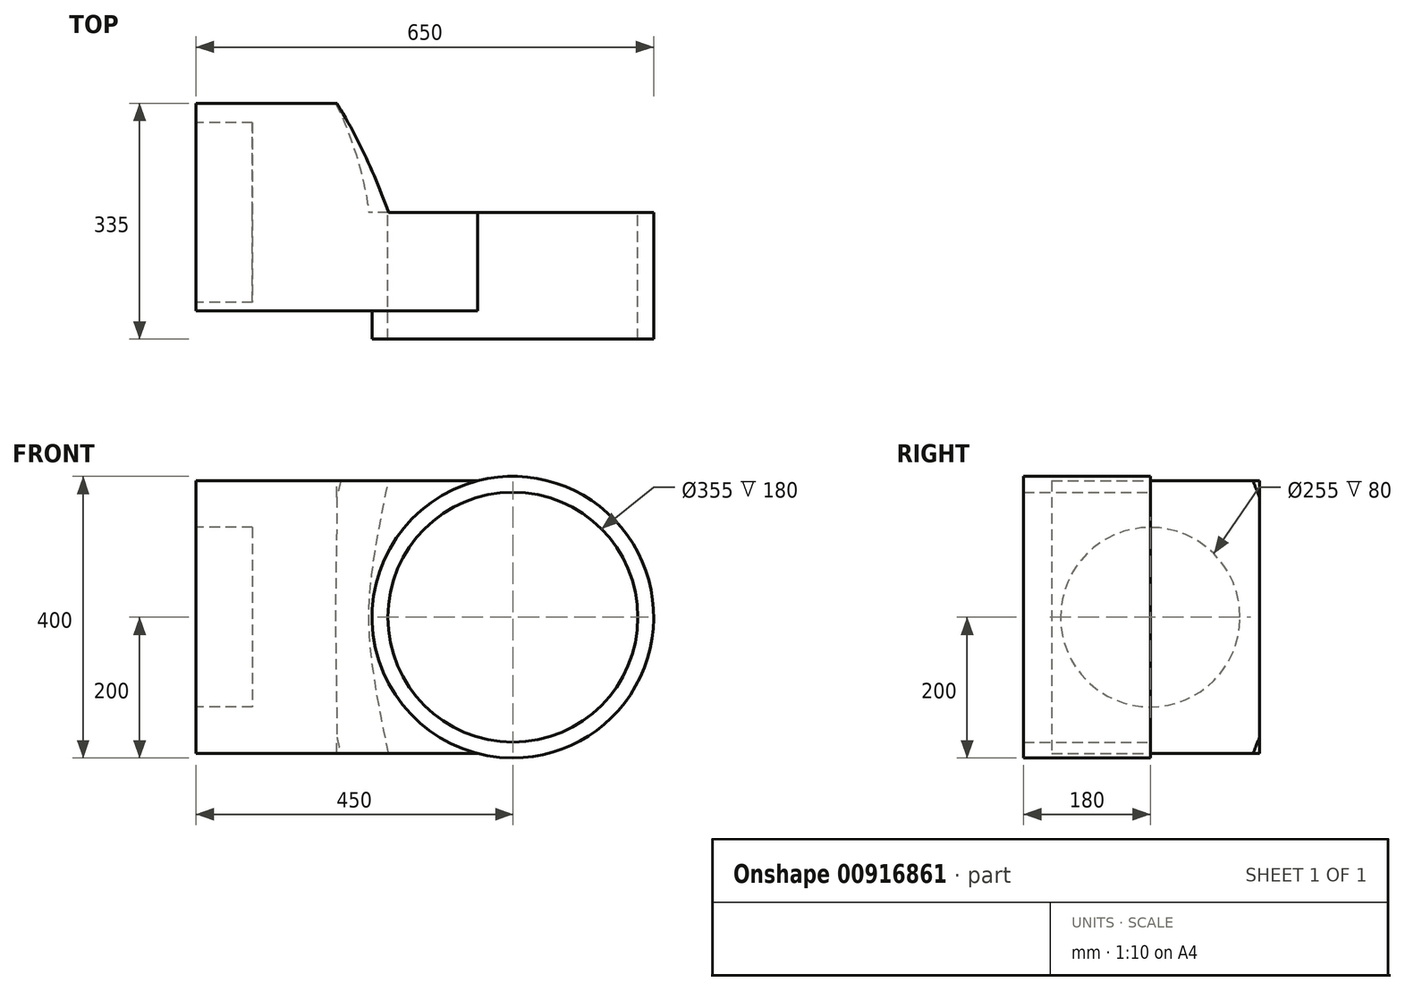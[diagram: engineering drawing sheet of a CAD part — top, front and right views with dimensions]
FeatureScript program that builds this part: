
annotation { "Feature Type Name" : "Feature", "Feature Type Description" : "" }
export const myFeature = defineFeature(function(context is Context, id is Id, definition is map)
    precondition{}
    {
        {
            var Q0;
            Q0=qCreatedBy(makeId("Front.planeOp"),FACE);
            var sketch = newSketch(context, id + "F0", { "sketchPlane" : qUnion([Q0])});
            skCircle(sketch, "E0", {"center": v(0, 0) * mm, "radius": 177.5 * mm});
            skCircle(sketch, "E1", {"center": v(0, 0) * mm, "radius": 200 * mm});
            skLineSegment(sketch, "E2.bottom", {"start": v(-50, 193.65) * mm, "end": v(-450, 193.65) * mm});
            skLineSegment(sketch, "E2.top", {"start": v(-50, -193.65) * mm, "end": v(-450, -193.65) * mm});
            skLineSegment(sketch, "E2.right", {"start": v(-450, 193.65) * mm, "end": v(-450, -193.65) * mm});
            skSolve(sketch);
        }
        {
            var Q0;
            {var subQ0=sQuery(id+"F0.wireOp",EDGE,"E2.bottom");Q0=makeQuery(id+"F0.imprint","IMPRINT",FACE,{"disambiguationData":[TD([[makeQuery(id+"F0.imprint","IMPRINT",EDGE,{"derivedFrom":subQ0}),1.0]])]});}
            extrude(context, id + "F1", {"entities" : qUnion([Q0]), "depth" : 140 * mm, "offsetDistance" : 25 * mm});
        }
        {
            var Q0;
            Q0=makeQuery(id+"F0.imprint","IMPRINT",FACE,{"disambiguationData":[TD([[makeQuery(id+"F0.imprint","IMPRINT",EDGE,{"derivedFrom":sQuery(id+"F0.wireOp",EDGE,"E0")}),-1.0]])]});
            extrude(context, id + "F2", {"entities" : qUnion([Q0]), "operationType" : NewBodyOperationType.ADD, "depth" : 180 * mm, "offsetDistance" : 25 * mm});
        }
        {
            var Q0;
            {var subQ0=sQuery(id+"F0.wireOp",EDGE,"E1");Q0=makeQuery(id+"F2.boolean.opBoolean","MERGE",FACE,{"derivedFrom":[makeQuery(id+"F1.opExtrude","CAP_FACE",FACE,{"disambiguationData":[OSD([subQ0,sQuery(id+"F0.wireOp",EDGE,"E2.bottom"),sQuery(id+"F0.wireOp",EDGE,"E2.top"),sQuery(id+"F0.wireOp",EDGE,"E2.right")])],"isStart":true}),makeQuery(id+"F2.opExtrude","CAP_FACE",FACE,{"disambiguationData":[OSD([sQuery(id+"F0.wireOp",EDGE,"E0"),subQ0])],"isStart":true})]});}
            var sketch = newSketch(context, id + "F3", { "sketchPlane" : qUnion([Q0])});
            skArc(sketch, "E3", {"start": v(50, -193.65) * mm, "mid": v(200, 0) * mm, "end": v(50, 193.65) * mm});
            skLineSegment(sketch, "E4", {"start": v(50, 193.65) * mm, "end": v(450, 193.65) * mm});
            skLineSegment(sketch, "E5", {"start": v(450, 193.65) * mm, "end": v(450, -193.65) * mm});
            skLineSegment(sketch, "E6", {"start": v(450, -193.65) * mm, "end": v(50, -193.65) * mm});
            skSolve(sketch);
        }
        {
            var Q0;
            Q0 = qSketchRegion(id + "F3", true);
            extrude(context, id + "F4", {"entities" : qUnion([Q0]), "operationType" : NewBodyOperationType.ADD, "depth" : 155 * mm, "offsetDistance" : 25 * mm});
        }
        {
            var Q0;
            Q0=makeQuery(id+"F4.boolean.opBoolean","MERGE",FACE,{"derivedFrom":[makeQuery(id+"F1.opExtrude","SWEPT_FACE",FACE,{"disambiguationData":[OSD([sQuery(id+"F0.wireOp",EDGE,"E2.bottom")])]}),makeQuery(id+"F4.opExtrude","SWEPT_FACE",FACE,{"disambiguationData":[OSD([sQuery(id+"F3.wireOp",EDGE,"E4")])]})]});
            var sketch = newSketch(context, id + "F5", { "sketchPlane" : qUnion([Q0])});
            skFitSpline(sketch, "E7", {"points": [v(-50, 0) * mm, v(-130.63, 35.3) * mm, v(-200.18, 84.2) * mm, v(-250, 155) * mm], "startDerivative": vector(-243.65, 97.7) * mm, "endDerivative": vector(-135.05, 226.7) * mm});
            skSolve(sketch);
        }
        {
            var Q0;
            Q0 = qSketchRegion(id + "F5", true);
            var Q1;
            {var subQ0=sQuery(id+"F5.wireOp",EDGE,"E7");Q1=makeQuery(id+"F5.imprint","IMPRINT",FACE,{"disambiguationData":[TD([[makeQuery(id+"F5.imprint","IMPRINT",EDGE,{"derivedFrom":subQ0}),-1.0]])]});}
            extrude(context, id + "F6", {"entities" : qUnion([Q0, Q1]), "operationType" : NewBodyOperationType.REMOVE, "oppositeDirection" : true, "depth" : 487 * mm, "offsetDistance" : 25 * mm});
        }
        {
            var Q0;
            Q0=makeQuery(id+"F6.boolean.opBoolean","INTERSECT",EDGE,{"derivedFrom":[makeQuery(id+"F4.opExtrude","SWEPT_FACE",FACE,{"disambiguationData":[OSD([sQuery(id+"F3.wireOp",EDGE,"E3")])]}),makeQuery(id+"F6.opExtrude","SWEPT_FACE",FACE,{"disambiguationData":[OSD([sQuery(id+"F5.wireOp",EDGE,"E7")])]})]});
            fillet(context, id + "F7", {"entities" : qUnion([Q0]), "radius" : 503.85 * mm, "tangentPropagation" : true, "allowEdgeOverflow" : false});
        }
        {
            var Q0;
            Q0=makeQuery(id+"F4.boolean.opBoolean","MERGE",FACE,{"derivedFrom":[makeQuery(id+"F1.opExtrude","SWEPT_FACE",FACE,{"disambiguationData":[OSD([sQuery(id+"F0.wireOp",EDGE,"E2.right")])]}),makeQuery(id+"F4.opExtrude","SWEPT_FACE",FACE,{"disambiguationData":[OSD([sQuery(id+"F3.wireOp",EDGE,"E5")])]})]});
            var sketch = newSketch(context, id + "F8", { "sketchPlane" : qUnion([Q0])});
            skCircle(sketch, "E8", {"center": v(0, 0) * mm, "radius": 127.5 * mm});
            skSolve(sketch);
        }
        {
            var Q0;
            Q0 = qSketchRegion(id + "F8", true);
            extrude(context, id + "F9", {"entities" : qUnion([Q0]), "operationType" : NewBodyOperationType.REMOVE, "oppositeDirection" : true, "depth" : 80 * mm, "offsetDistance" : 25 * mm});
        }
    });
